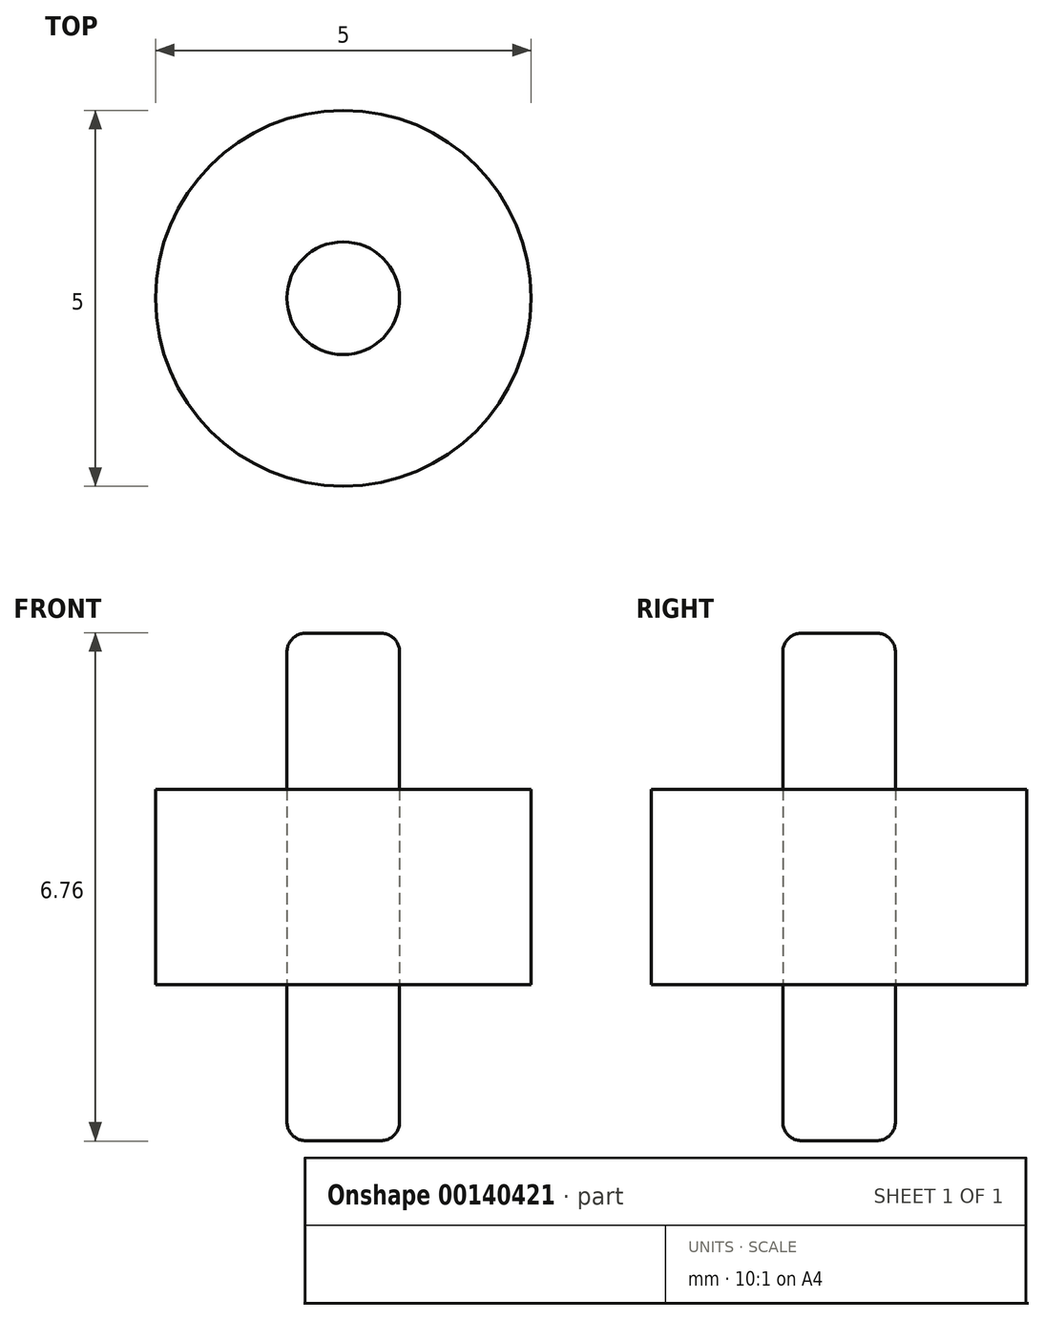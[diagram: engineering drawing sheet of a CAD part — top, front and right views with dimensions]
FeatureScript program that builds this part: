
annotation { "Feature Type Name" : "Feature", "Feature Type Description" : "" }
export const myFeature = defineFeature(function(context is Context, id is Id, definition is map)
    precondition{}
    {
        {
            var Q0;
            Q0=qCreatedBy(makeId("Top.planeOp"),FACE);
            var sketch = newSketch(context, id + "F0", { "sketchPlane" : qUnion([Q0])});
            skCircle(sketch, "E0", {"center": v(0, 0) * mm, "radius": 2.5 * mm});
            skCircle(sketch, "E1", {"center": v(0, 0) * mm, "radius": 0.75 * mm});
            skSolve(sketch);
        }
        {
            var Q0;
            Q0 = qSketchRegion(id + "F0", true);
            extrude(context, id + "F1", {"entities" : qUnion([Q0]), "endBound" : BoundingType.SYMMETRIC, "depth" : 2.6 * mm});
        }
        {
            var Q0;
            Q0=qCreatedBy(makeId("Top.planeOp"),FACE);
            var sketch = newSketch(context, id + "F2", { "sketchPlane" : qUnion([Q0])});
            skCircle(sketch, "E2", {"center": v(0, 0) * mm, "radius": 0.75 * mm});
            skSolve(sketch);
        }
        {
            var Q0;
            Q0 = qSketchRegion(id + "F2", true);
            extrude(context, id + "F3", {"entities" : qUnion([Q0]), "endBound" : BoundingType.SYMMETRIC, "depth" : 6.75 * mm});
        }
        {
            var Q0;
            Q0=makeQuery(id+"F3.opExtrude","CAP_FACE",FACE,{"disambiguationData":[OSD([sQuery(id+"F2.wireOp",EDGE,"E2")])],"isStart":true});
            var Q1;
            Q1=makeQuery(id+"F3.opExtrude","CAP_FACE",FACE,{"disambiguationData":[OSD([sQuery(id+"F2.wireOp",EDGE,"E2")])],"isStart":false});
            fillet(context, id + "F4", {"entities" : qUnion([Q0, Q1]), "radius" : 0.25 * mm, "tangentPropagation" : true, "allowEdgeOverflow" : false});
        }
    });
